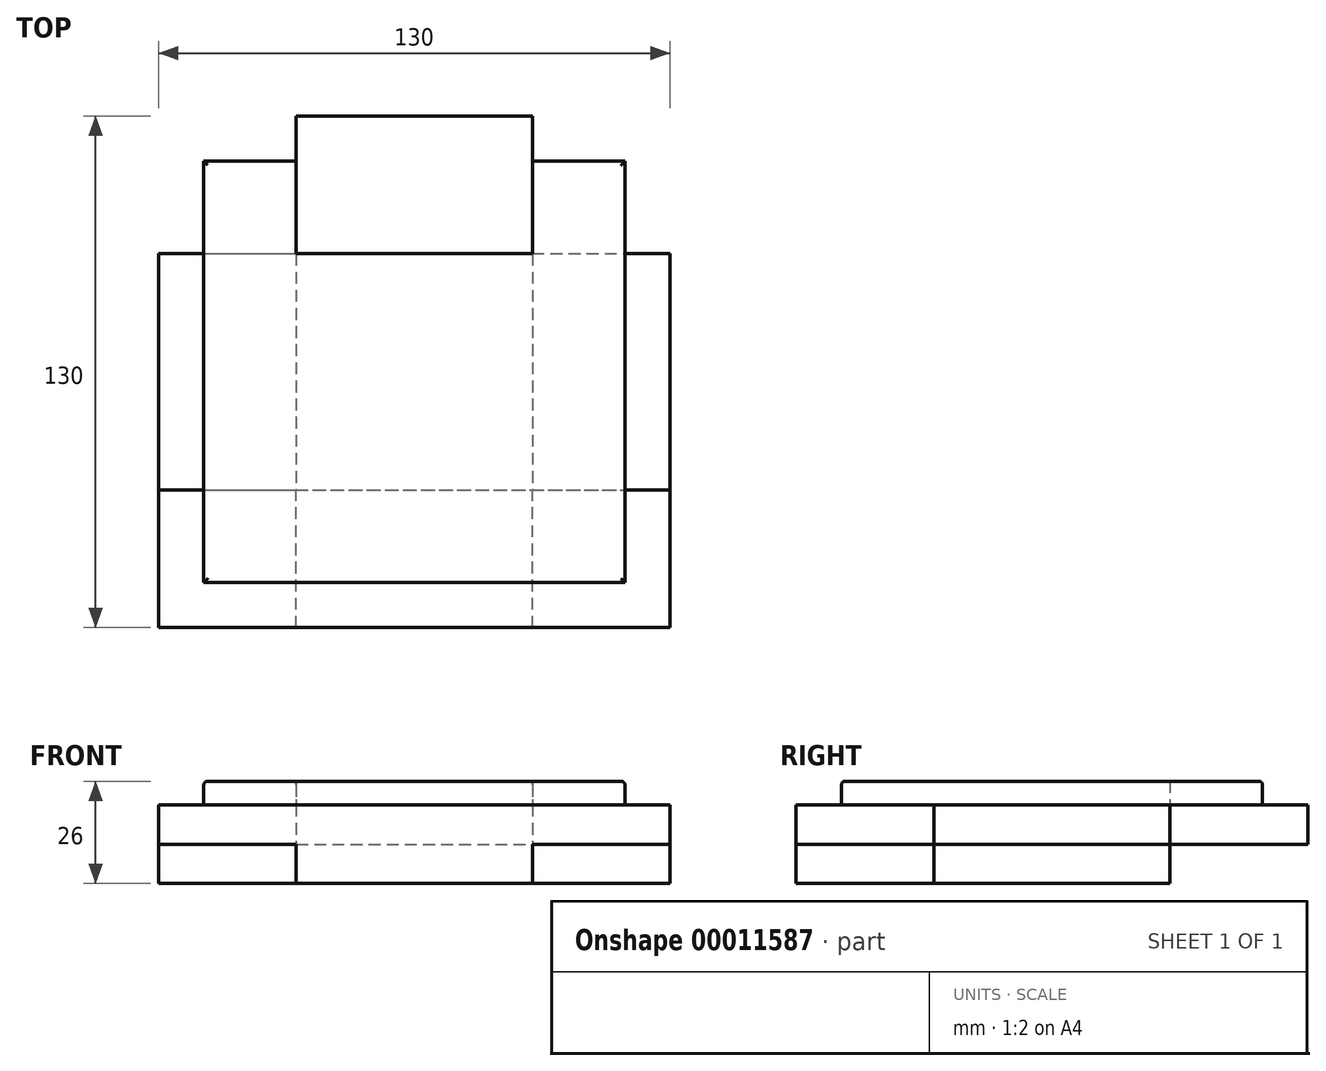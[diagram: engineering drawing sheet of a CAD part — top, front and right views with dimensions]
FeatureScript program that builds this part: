
annotation { "Feature Type Name" : "Feature", "Feature Type Description" : "" }
export const myFeature = defineFeature(function(context is Context, id is Id, definition is map)
    precondition{}
    {
        {
            var Q0;
            Q0=qCreatedBy(makeId("Top.planeOp"),FACE);
            var sketch = newSketch(context, id + "F0", { "sketchPlane" : qUnion([Q0])});
            skLineSegment(sketch, "E0.rect.bottom", {"start": v(65, -65) * mm, "end": v(-65, -65) * mm, "construction": true});
            skLineSegment(sketch, "E0.rect.top", {"start": v(65, 65) * mm, "end": v(-65, 65) * mm, "construction": true});
            skLineSegment(sketch, "E0.rect.left", {"start": v(65, -65) * mm, "end": v(65, 65) * mm, "construction": true});
            skLineSegment(sketch, "E0.rect.right", {"start": v(-65, -65) * mm, "end": v(-65, 65) * mm, "construction": true});
            skPoint(sketch, "E0.rect.middle", {"position": v(0, 0) * mm});
            skLineSegment(sketch, "E1.bottom", {"start": v(-65, -65) * mm, "end": v(65, -65) * mm});
            skLineSegment(sketch, "E1.top", {"start": v(-65, -30) * mm, "end": v(65, -30) * mm});
            skLineSegment(sketch, "E1.left", {"start": v(-65, -65) * mm, "end": v(-65, -30) * mm});
            skLineSegment(sketch, "E1.right", {"start": v(65, -65) * mm, "end": v(65, -30) * mm});
            skLineSegment(sketch, "E2.bottom", {"start": v(-65, 65) * mm, "end": v(-30, 65) * mm});
            skLineSegment(sketch, "E2.top", {"start": v(-65, -65) * mm, "end": v(-30, -65) * mm});
            skLineSegment(sketch, "E2.left", {"start": v(-65, 65) * mm, "end": v(-65, -65) * mm});
            skLineSegment(sketch, "E2.right", {"start": v(-30, 65) * mm, "end": v(-30, -65) * mm});
            skLineSegment(sketch, "E3.bottom", {"start": v(65, 65) * mm, "end": v(30, 65) * mm});
            skLineSegment(sketch, "E3.top", {"start": v(65, -65) * mm, "end": v(30, -65) * mm});
            skLineSegment(sketch, "E3.left", {"start": v(65, 65) * mm, "end": v(65, -65) * mm});
            skLineSegment(sketch, "E3.right", {"start": v(30, 65) * mm, "end": v(30, -65) * mm});
            skLineSegment(sketch, "E4.bottom", {"start": v(-65, 65) * mm, "end": v(65, 65) * mm});
            skLineSegment(sketch, "E4.top", {"start": v(-65, 30) * mm, "end": v(65, 30) * mm});
            skLineSegment(sketch, "E4.left", {"start": v(-65, 65) * mm, "end": v(-65, 30) * mm});
            skLineSegment(sketch, "E4.right", {"start": v(65, 65) * mm, "end": v(65, 30) * mm});
            skSolve(sketch);
        }
        {
            var Q0;
            {var subQ0=sQuery(id+"F0.wireOp",EDGE,"E2.left");var subQ1=sQuery(id+"F0.wireOp",EDGE,"E1.top");var subQ2=makeQuery(id+"F0.imprint","INTERSECT",VERTEX,{"derivedFrom":[subQ1,subQ0]});Q0=makeQuery(id+"F0.imprint","IMPRINT",FACE,{"disambiguationData":[TD([[makeQuery(id+"F0.imprint","IMPRINT",EDGE,{"disambiguationData":[TD([[subQ2,-1.0]])],"derivedFrom":subQ1}),1.0]])]});}
            var Q1;
            {var subQ5=sQuery(id+"F0.wireOp",EDGE,"E4.left");Q1=makeQuery(id+"F0.imprint","IMPRINT",FACE,{"disambiguationData":[TD([[makeQuery(id+"F0.imprint","IMPRINT",EDGE,{"derivedFrom":subQ5}),1.0]])]});}
            var Q2;
            {var subQ5=sQuery(id+"F0.wireOp",EDGE,"E2.top");Q2=makeQuery(id+"F0.imprint","IMPRINT",FACE,{"disambiguationData":[TD([[makeQuery(id+"F0.imprint","IMPRINT",EDGE,{"derivedFrom":subQ5}),1.0]])]});}
            extrude(context, id + "F1", {"entities" : qUnion([Q0, Q1, Q2]), "depth" : 20 * mm});
        }
        {
            var Q0;
            {var subQ5=sQuery(id+"F0.wireOp",EDGE,"E4.right");Q0=makeQuery(id+"F0.imprint","IMPRINT",FACE,{"disambiguationData":[TD([[makeQuery(id+"F0.imprint","IMPRINT",EDGE,{"derivedFrom":subQ5}),-1.0]])]});}
            var Q1;
            {var subQ0=sQuery(id+"F0.wireOp",EDGE,"E3.left");var subQ1=sQuery(id+"F0.wireOp",EDGE,"E1.top");var subQ2=makeQuery(id+"F0.imprint","INTERSECT",VERTEX,{"derivedFrom":[subQ1,subQ0]});Q1=makeQuery(id+"F0.imprint","IMPRINT",FACE,{"disambiguationData":[TD([[makeQuery(id+"F0.imprint","IMPRINT",EDGE,{"disambiguationData":[TD([[subQ2,1.0]])],"derivedFrom":subQ1}),1.0]])]});}
            var Q2;
            {var subQ5=sQuery(id+"F0.wireOp",EDGE,"E3.top");Q2=makeQuery(id+"F0.imprint","IMPRINT",FACE,{"disambiguationData":[TD([[makeQuery(id+"F0.imprint","IMPRINT",EDGE,{"derivedFrom":subQ5}),-1.0]])]});}
            extrude(context, id + "F2", {"entities" : qUnion([Q0, Q1, Q2]), "depth" : 20 * mm});
        }
        {
            var Q0;
            Q0=makeQuery(id+"F1.opExtrude","CAP_FACE",FACE,{"disambiguationData":[OSD([sQuery(id+"F0.wireOp",EDGE,"E2.top"),sQuery(id+"F0.wireOp",EDGE,"E2.left"),sQuery(id+"F0.wireOp",EDGE,"E2.right"),sQuery(id+"F0.wireOp",EDGE,"E4.bottom"),sQuery(id+"F0.wireOp",EDGE,"E4.left")])],"isStart":false});
            var sketch = newSketch(context, id + "F3", { "sketchPlane" : qUnion([Q0])});
            skLineSegment(sketch, "E5", {"start": v(-30, 30) * mm, "end": v(-65, 30) * mm});
            skLineSegment(sketch, "E6", {"start": v(-30, -30) * mm, "end": v(-65, -30) * mm});
            skSolve(sketch);
        }
        {
            var Q0;
            Q0 = qSketchRegion(id + "F3", true);
            var Q1;
            {var subQ0=sQuery(id+"F3.wireOp",EDGE,"E5");Q1=makeQuery(id+"F3.imprint","IMPRINT",FACE,{"disambiguationData":[TD([[makeQuery(id+"F3.imprint","IMPRINT",EDGE,{"derivedFrom":subQ0}),-1.0]])]});}
            var Q2;
            {var subQ0=sQuery(id+"F3.wireOp",EDGE,"E6");Q2=makeQuery(id+"F3.imprint","IMPRINT",FACE,{"disambiguationData":[TD([[makeQuery(id+"F3.imprint","IMPRINT",EDGE,{"derivedFrom":subQ0}),1.0]])]});}
            extrude(context, id + "F4", {"entities" : qUnion([Q0, Q1, Q2]), "operationType" : NewBodyOperationType.REMOVE, "oppositeDirection" : true, "depth" : 10 * mm});
        }
        {
            var Q0;
            Q0=makeQuery(id+"F2.opExtrude","CAP_FACE",FACE,{"disambiguationData":[OSD([sQuery(id+"F0.wireOp",EDGE,"E3.top"),sQuery(id+"F0.wireOp",EDGE,"E3.left"),sQuery(id+"F0.wireOp",EDGE,"E3.right"),sQuery(id+"F0.wireOp",EDGE,"E4.bottom"),sQuery(id+"F0.wireOp",EDGE,"E4.right")])],"isStart":false});
            var sketch = newSketch(context, id + "F5", { "sketchPlane" : qUnion([Q0])});
            skLineSegment(sketch, "E7", {"start": v(65, 30) * mm, "end": v(30, 30) * mm});
            skLineSegment(sketch, "E8", {"start": v(65, -30) * mm, "end": v(30, -30) * mm});
            skSolve(sketch);
        }
        {
            var Q0;
            {var subQ0=sQuery(id+"F5.wireOp",EDGE,"E7");Q0=makeQuery(id+"F5.imprint","IMPRINT",FACE,{"disambiguationData":[TD([[makeQuery(id+"F5.imprint","IMPRINT",EDGE,{"derivedFrom":subQ0}),-1.0]])]});}
            var Q1;
            {var subQ0=sQuery(id+"F5.wireOp",EDGE,"E8");Q1=makeQuery(id+"F5.imprint","IMPRINT",FACE,{"disambiguationData":[TD([[makeQuery(id+"F5.imprint","IMPRINT",EDGE,{"derivedFrom":subQ0}),1.0]])]});}
            extrude(context, id + "F6", {"entities" : qUnion([Q0, Q1]), "operationType" : NewBodyOperationType.REMOVE, "oppositeDirection" : true, "depth" : 10 * mm});
        }
        {
            var Q0;
            {var subQ0=sQuery(id+"F0.wireOp",EDGE,"E1.bottom");Q0=makeQuery(id+"F0.imprint","IMPRINT",FACE,{"disambiguationData":[TD([[makeQuery(id+"F0.imprint","IMPRINT",EDGE,{"derivedFrom":subQ0}),1.0]])]});}
            var Q1;
            {var subQ5=sQuery(id+"F0.wireOp",EDGE,"E2.top");Q1=makeQuery(id+"F0.imprint","IMPRINT",FACE,{"disambiguationData":[TD([[makeQuery(id+"F0.imprint","IMPRINT",EDGE,{"derivedFrom":subQ5}),1.0]])]});}
            var Q2;
            {var subQ5=sQuery(id+"F0.wireOp",EDGE,"E3.top");Q2=makeQuery(id+"F0.imprint","IMPRINT",FACE,{"disambiguationData":[TD([[makeQuery(id+"F0.imprint","IMPRINT",EDGE,{"derivedFrom":subQ5}),-1.0]])]});}
            extrude(context, id + "F7", {"entities" : qUnion([Q0, Q1, Q2]), "depth" : 20 * mm});
        }
        {
            var Q0;
            {var subQ5=sQuery(id+"F0.wireOp",EDGE,"E4.right");Q0=makeQuery(id+"F0.imprint","IMPRINT",FACE,{"disambiguationData":[TD([[makeQuery(id+"F0.imprint","IMPRINT",EDGE,{"derivedFrom":subQ5}),-1.0]])]});}
            var Q1;
            {var subQ0=sQuery(id+"F0.wireOp",EDGE,"E4.bottom");var subQ1=sQuery(id+"F0.wireOp",EDGE,"E2.right");var subQ2=makeQuery(id+"F0.imprint","INTERSECT",VERTEX,{"derivedFrom":[subQ1,subQ0]});Q1=makeQuery(id+"F0.imprint","IMPRINT",FACE,{"disambiguationData":[TD([[makeQuery(id+"F0.imprint","IMPRINT",EDGE,{"disambiguationData":[TD([[subQ2,-1.0]])],"derivedFrom":subQ1}),1.0]])]});}
            var Q2;
            {var subQ5=sQuery(id+"F0.wireOp",EDGE,"E4.left");Q2=makeQuery(id+"F0.imprint","IMPRINT",FACE,{"disambiguationData":[TD([[makeQuery(id+"F0.imprint","IMPRINT",EDGE,{"derivedFrom":subQ5}),1.0]])]});}
            extrude(context, id + "F8", {"entities" : qUnion([Q0, Q1, Q2]), "depth" : 20 * mm});
        }
        {
            var Q0;
            Q0=makeQuery(id+"F7.opExtrude","CAP_FACE",FACE,{"disambiguationData":[OSD([sQuery(id+"F0.wireOp",EDGE,"E1.bottom"),sQuery(id+"F0.wireOp",EDGE,"E1.top"),sQuery(id+"F0.wireOp",EDGE,"E2.top"),sQuery(id+"F0.wireOp",EDGE,"E2.left"),sQuery(id+"F0.wireOp",EDGE,"E3.top"),sQuery(id+"F0.wireOp",EDGE,"E3.left")])],"isStart":true});
            var sketch = newSketch(context, id + "F9", { "sketchPlane" : qUnion([Q0])});
            skLineSegment(sketch, "E9", {"start": v(-30, 65) * mm, "end": v(-30, 30) * mm});
            skLineSegment(sketch, "E10", {"start": v(30, 65) * mm, "end": v(30, 30) * mm});
            skSolve(sketch);
        }
        {
            var Q0;
            Q0 = qSketchRegion(id + "F9", true);
            var Q1;
            {var subQ0=sQuery(id+"F9.wireOp",EDGE,"E9");Q1=makeQuery(id+"F9.imprint","IMPRINT",FACE,{"disambiguationData":[TD([[makeQuery(id+"F9.imprint","IMPRINT",EDGE,{"derivedFrom":subQ0}),-1.0]])]});}
            var Q2;
            {var subQ0=sQuery(id+"F9.wireOp",EDGE,"E10");Q2=makeQuery(id+"F9.imprint","IMPRINT",FACE,{"disambiguationData":[TD([[makeQuery(id+"F9.imprint","IMPRINT",EDGE,{"derivedFrom":subQ0}),1.0]])]});}
            extrude(context, id + "F10", {"entities" : qUnion([Q0, Q1, Q2]), "operationType" : NewBodyOperationType.REMOVE, "oppositeDirection" : true, "depth" : 10 * mm});
        }
        {
            var Q0;
            Q0=makeQuery(id+"F8.opExtrude","CAP_FACE",FACE,{"disambiguationData":[OSD([sQuery(id+"F0.wireOp",EDGE,"E4.bottom"),sQuery(id+"F0.wireOp",EDGE,"E4.top"),sQuery(id+"F0.wireOp",EDGE,"E4.left"),sQuery(id+"F0.wireOp",EDGE,"E4.right")])],"isStart":true});
            var sketch = newSketch(context, id + "F11", { "sketchPlane" : qUnion([Q0])});
            skLineSegment(sketch, "E11", {"start": v(-30, -30) * mm, "end": v(-30, -65) * mm});
            skLineSegment(sketch, "E12", {"start": v(30, -30) * mm, "end": v(30, -65) * mm});
            skSolve(sketch);
        }
        {
            var Q0;
            {var subQ0=sQuery(id+"F11.wireOp",EDGE,"E11");Q0=makeQuery(id+"F11.imprint","IMPRINT",FACE,{"disambiguationData":[TD([[makeQuery(id+"F11.imprint","IMPRINT",EDGE,{"derivedFrom":subQ0}),-1.0]])]});}
            var Q1;
            {var subQ0=sQuery(id+"F11.wireOp",EDGE,"E12");Q1=makeQuery(id+"F11.imprint","IMPRINT",FACE,{"disambiguationData":[TD([[makeQuery(id+"F11.imprint","IMPRINT",EDGE,{"derivedFrom":subQ0}),1.0]])]});}
            extrude(context, id + "F12", {"entities" : qUnion([Q0, Q1]), "operationType" : NewBodyOperationType.REMOVE, "oppositeDirection" : true, "depth" : 10 * mm});
        }
        {
            var Q0;
            Q0=makeQuery(id+"F8.opExtrude","CAP_FACE",FACE,{"disambiguationData":[OSD([sQuery(id+"F0.wireOp",EDGE,"E4.bottom"),sQuery(id+"F0.wireOp",EDGE,"E4.top"),sQuery(id+"F0.wireOp",EDGE,"E4.left"),sQuery(id+"F0.wireOp",EDGE,"E4.right")])],"isStart":false});
            var sketch = newSketch(context, id + "F13", { "sketchPlane" : qUnion([Q0])});
            skLineSegment(sketch, "E13.bottom", {"start": v(53.5, 53.5) * mm, "end": v(-53.5, 53.5) * mm});
            skLineSegment(sketch, "E13.top", {"start": v(53.5, -53.5) * mm, "end": v(-53.5, -53.5) * mm});
            skLineSegment(sketch, "E13.left", {"start": v(53.5, 53.5) * mm, "end": v(53.5, -53.5) * mm});
            skLineSegment(sketch, "E13.right", {"start": v(-53.5, 53.5) * mm, "end": v(-53.5, -53.5) * mm});
            skPoint(sketch, "E13.middle", {"position": v(0, 0) * mm});
            skSolve(sketch);
        }
        {
            var Q0;
            {var subQ0=sQuery(id+"F13.wireOp",EDGE,"E13.bottom");Q0=makeQuery(id+"F13.imprint","IMPRINT",FACE,{"disambiguationData":[TD([[makeQuery(id+"F13.imprint","IMPRINT",EDGE,{"derivedFrom":subQ0}),1.0]])]});}
            var Q1;
            {var subQ0=sQuery(id+"F13.wireOp",EDGE,"E13.top");Q1=makeQuery(id+"F13.imprint","IMPRINT",FACE,{"disambiguationData":[TD([[makeQuery(id+"F13.imprint","IMPRINT",EDGE,{"derivedFrom":subQ0}),-1.0]])]});}
            extrude(context, id + "F14", {"entities" : qUnion([Q0, Q1]), "depth" : 6 * mm});
        }
        {
            var Q0;
            Q0=makeQuery(id+"F14.opExtrude","CAP_EDGE",EDGE,{"disambiguationData":[OSD([sQuery(id+"F13.wireOp",EDGE,"E13.bottom")])],"isStart":false});
            var Q1;
            Q1=makeQuery(id+"F14.opExtrude","CAP_EDGE",EDGE,{"disambiguationData":[OSD([sQuery(id+"F13.wireOp",EDGE,"E13.left")])],"isStart":false});
            var Q2;
            Q2=makeQuery(id+"F14.opExtrude","CAP_EDGE",EDGE,{"disambiguationData":[OSD([sQuery(id+"F13.wireOp",EDGE,"E13.top")])],"isStart":false});
            var Q3;
            Q3=makeQuery(id+"F14.opExtrude","CAP_EDGE",EDGE,{"disambiguationData":[OSD([sQuery(id+"F13.wireOp",EDGE,"E13.right")])],"isStart":false});
            fillet(context, id + "F15", {"entities" : qUnion([Q0, Q1, Q2, Q3]), "radius" : 1 * mm, "tangentPropagation" : true, "allowEdgeOverflow" : false});
        }
    });
